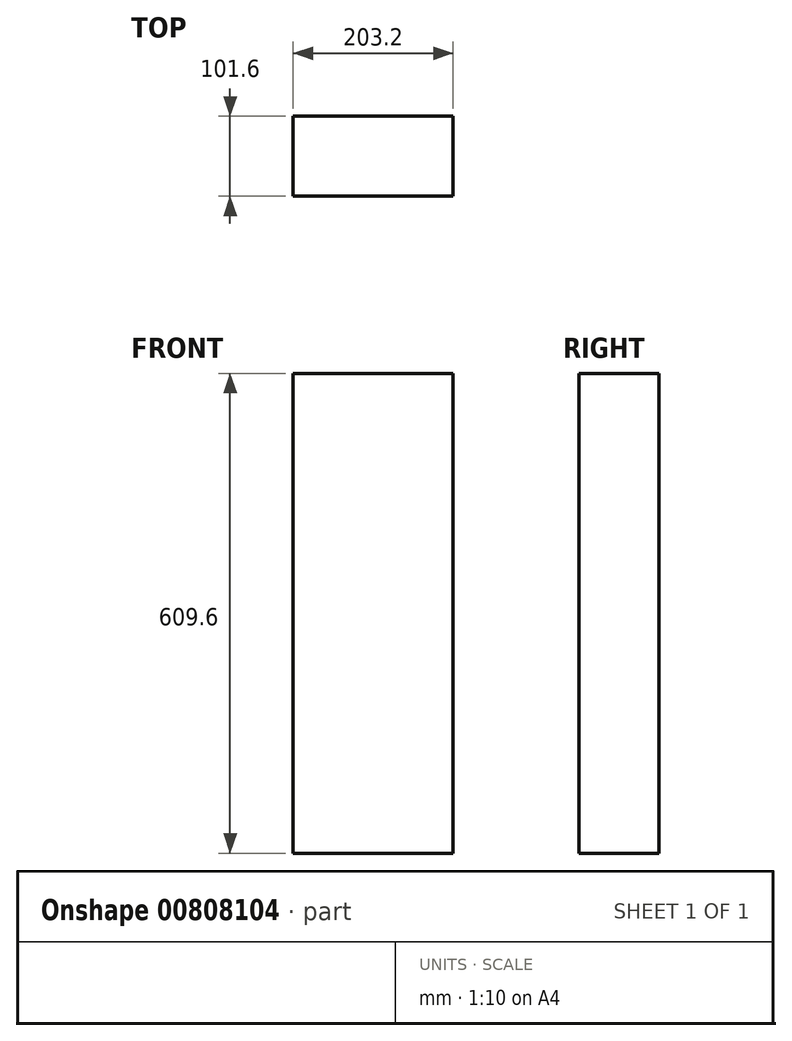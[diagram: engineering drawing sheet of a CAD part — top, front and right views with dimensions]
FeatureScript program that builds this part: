
annotation { "Feature Type Name" : "Feature", "Feature Type Description" : "" }
export const myFeature = defineFeature(function(context is Context, id is Id, definition is map)
    precondition{}
    {
        {
            var Q0;
            Q0=qCreatedBy(makeId("Front.planeOp"),FACE);
            var sketch = newSketch(context, id + "F0", { "sketchPlane" : qUnion([Q0])});
            skLineSegment(sketch, "E0.bottom", {"start": v(101.6, 304.8) * mm, "end": v(-101.6, 304.8) * mm});
            skLineSegment(sketch, "E0.top", {"start": v(101.6, -304.8) * mm, "end": v(-101.6, -304.8) * mm});
            skLineSegment(sketch, "E0.left", {"start": v(101.6, 304.8) * mm, "end": v(101.6, -304.8) * mm});
            skLineSegment(sketch, "E0.right", {"start": v(-101.6, 304.8) * mm, "end": v(-101.6, -304.8) * mm});
            skPoint(sketch, "E0.middle", {"position": v(0, 0) * mm});
            skSolve(sketch);
        }
        {
            var Q0;
            Q0=qSketchRegion(id+"F0",true);
            extrude(context, id + "F1", {"entities" : qUnion([Q0]), "depth" : 101.6 * mm, "offsetDistance" : 25.4 * mm});
        }
    });
